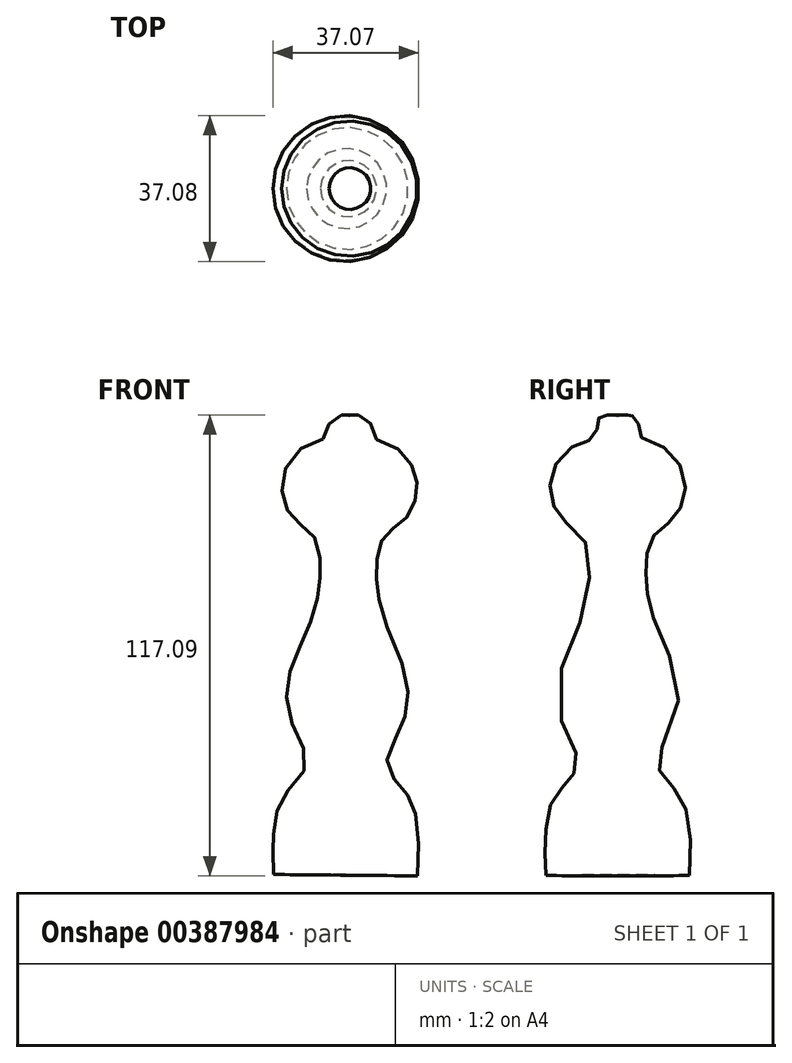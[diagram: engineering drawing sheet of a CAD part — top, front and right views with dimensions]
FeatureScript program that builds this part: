
annotation { "Feature Type Name" : "Feature", "Feature Type Description" : "" }
export const myFeature = defineFeature(function(context is Context, id is Id, definition is map)
    precondition{}
    {
        {
            var Q0;
            Q0=qCreatedBy(makeId("Front.planeOp"),FACE);
            var sketch = newSketch(context, id + "F0", { "sketchPlane" : qUnion([Q0])});
            skFitSpline(sketch, "E0", {"points": [v(-32.24, -42.8) * mm, v(-32.44, -36.24) * mm, v(-31.95, -29.84) * mm, v(-29.37, -22.35) * mm, v(-23.95, -15.07) * mm, v(-26.97, -6) * mm, v(-28.94, 4.6) * mm, v(-25.91, 14.37) * mm, v(-21.9, 24.15) * mm, v(-20.5, 31.61) * mm, v(-20.44, 37.11) * mm, v(-22.17, 43.33) * mm, v(-26.53, 47.02) * mm, v(-29.48, 51.56) * mm, v(-29.92, 58.34) * mm, v(-24.66, 65.82) * mm, v(-18.43, 68.91) * mm, v(-17.73, 73.16) * mm, v(-12.84, 73.67) * mm], "startDerivative": vector(-10.1, 328.91) * mm, "endDerivative": vector(88.05, -23.22) * mm});
            skLineSegment(sketch, "E1", {"start": v(-32.24, -42.8) * mm, "end": v(-13.97, -42.8) * mm});
            skLineSegment(sketch, "E2", {"start": v(-13.97, -42.8) * mm, "end": v(-12.84, 73.67) * mm});
            skSolve(sketch);
        }
        {
            var Q0;
            Q0=makeQuery(id+"F0.imprint","IMPRINT",FACE,{"disambiguationData":[TD([[makeQuery(id+"F0.imprint","IMPRINT",EDGE,{"derivedFrom":sQuery(id+"F0.wireOp",EDGE,"E0")}),-1.0]])]});
            var Q1;
            Q1=sQuery(id+"F0.wireOp",EDGE,"E2");
            revolve(context, id + "F1", {"entities" : qUnion([Q0]), "axis" : qUnion([Q1]), "revolveType" : RevolveType.FULL});
        }
    });
